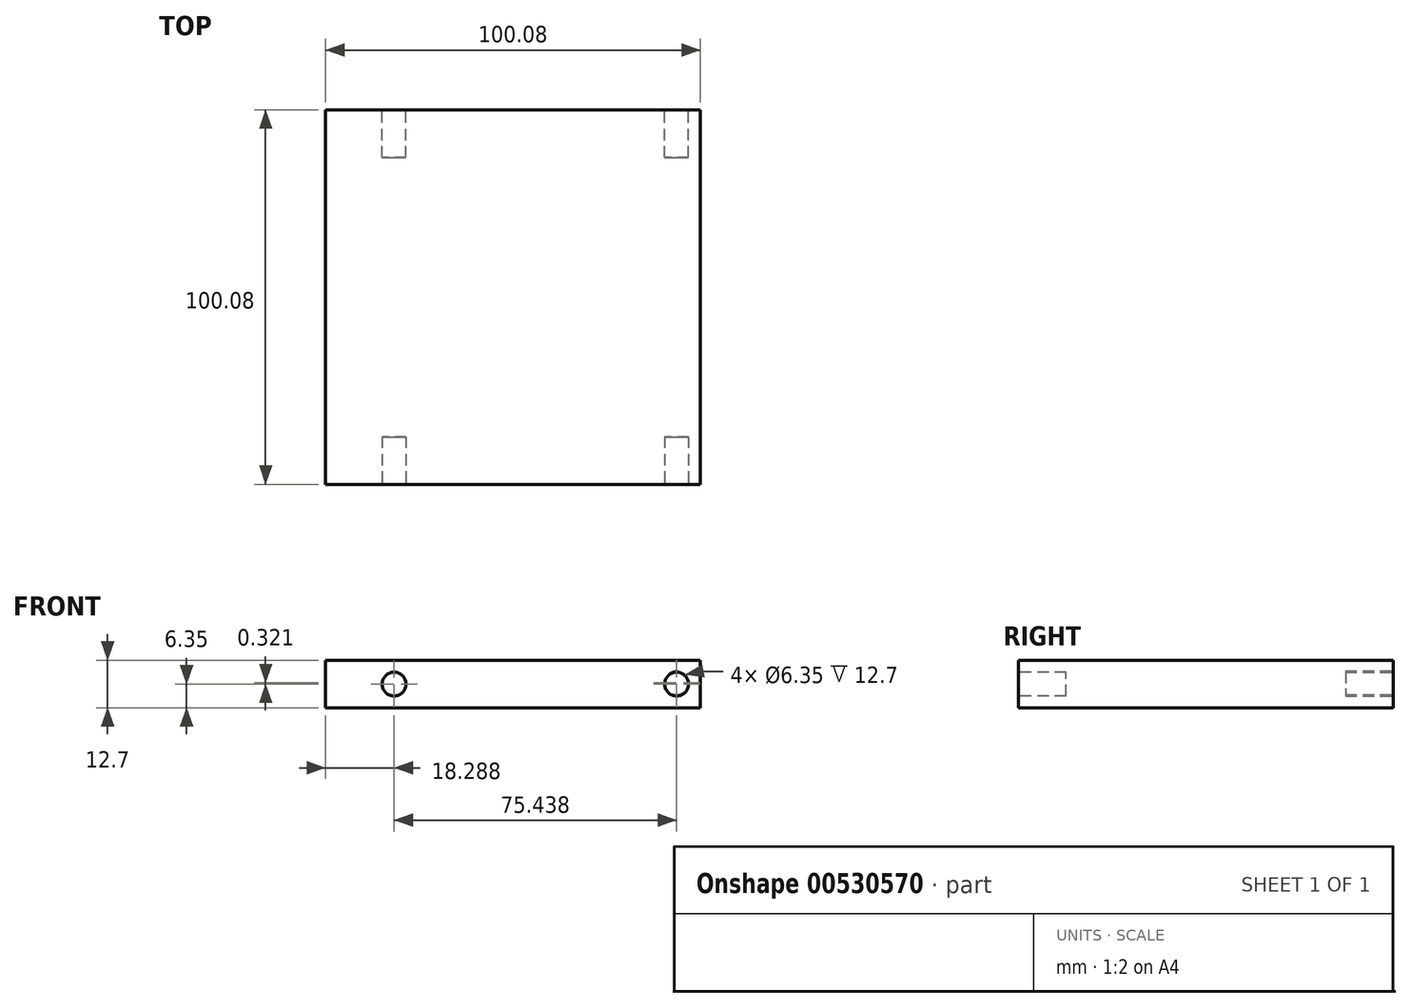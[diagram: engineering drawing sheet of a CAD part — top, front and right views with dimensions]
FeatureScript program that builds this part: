
annotation { "Feature Type Name" : "Feature", "Feature Type Description" : "" }
export const myFeature = defineFeature(function(context is Context, id is Id, definition is map)
    precondition{}
    {
        {
            var Q0;
            Q0=qCreatedBy(makeId("Top.planeOp"),FACE);
            var sketch = newSketch(context, id + "F0", { "sketchPlane" : qUnion([Q0])});
            skLineSegment(sketch, "E0.bottom", {"start": v(0, 0) * mm, "end": v(100.08, 0) * mm});
            skLineSegment(sketch, "E0.top", {"start": v(0, -100.08) * mm, "end": v(100.08, -100.08) * mm});
            skLineSegment(sketch, "E0.left", {"start": v(0, 0) * mm, "end": v(0, -100.08) * mm});
            skLineSegment(sketch, "E0.right", {"start": v(100.08, 0) * mm, "end": v(100.08, -100.08) * mm});
            skSolve(sketch);
        }
        {
            var Q0;
            Q0 = qSketchRegion(id + "F0", true);
            extrude(context, id + "F1", {"entities" : qUnion([Q0]), "depth" : 12.7 * mm, "offsetDistance" : 25.4 * mm});
        }
        {
            var Q0;
            Q0=makeQuery(id+"F1.opExtrude","SWEPT_FACE",FACE,{"disambiguationData":[OSD([sQuery(id+"F0.wireOp",EDGE,"E0.top")])]});
            var sketch = newSketch(context, id + "F2", { "sketchPlane" : qUnion([Q0])});
            skCircle(sketch, "E1", {"center": v(93.73, 6.35) * mm, "radius": 3.18 * mm});
            skCircle(sketch, "E2", {"center": v(18.29, 6.35) * mm, "radius": 3.18 * mm});
            skSolve(sketch);
        }
        {
            var Q0;
            Q0 = qSketchRegion(id + "F2", true);
            extrude(context, id + "F3", {"entities" : qUnion([Q0]), "operationType" : NewBodyOperationType.REMOVE, "oppositeDirection" : true, "depth" : 12.7 * mm, "offsetDistance" : 25.4 * mm});
        }
        {
            var Q0;
            Q0=makeQuery(id+"F1.opExtrude","SWEPT_FACE",FACE,{"disambiguationData":[OSD([sQuery(id+"F0.wireOp",EDGE,"E0.bottom")])]});
            var sketch = newSketch(context, id + "F4", { "sketchPlane" : qUnion([Q0])});
            skCircle(sketch, "E3", {"center": v(-93.73, 6.67) * mm, "radius": 3.18 * mm});
            skCircle(sketch, "E4", {"center": v(-18.29, 6.35) * mm, "radius": 3.18 * mm});
            skSolve(sketch);
        }
        {
            var Q0;
            Q0 = qSketchRegion(id + "F4", true);
            extrude(context, id + "F5", {"entities" : qUnion([Q0]), "operationType" : NewBodyOperationType.REMOVE, "oppositeDirection" : true, "depth" : 12.7 * mm, "offsetDistance" : 25.4 * mm});
        }
    });
